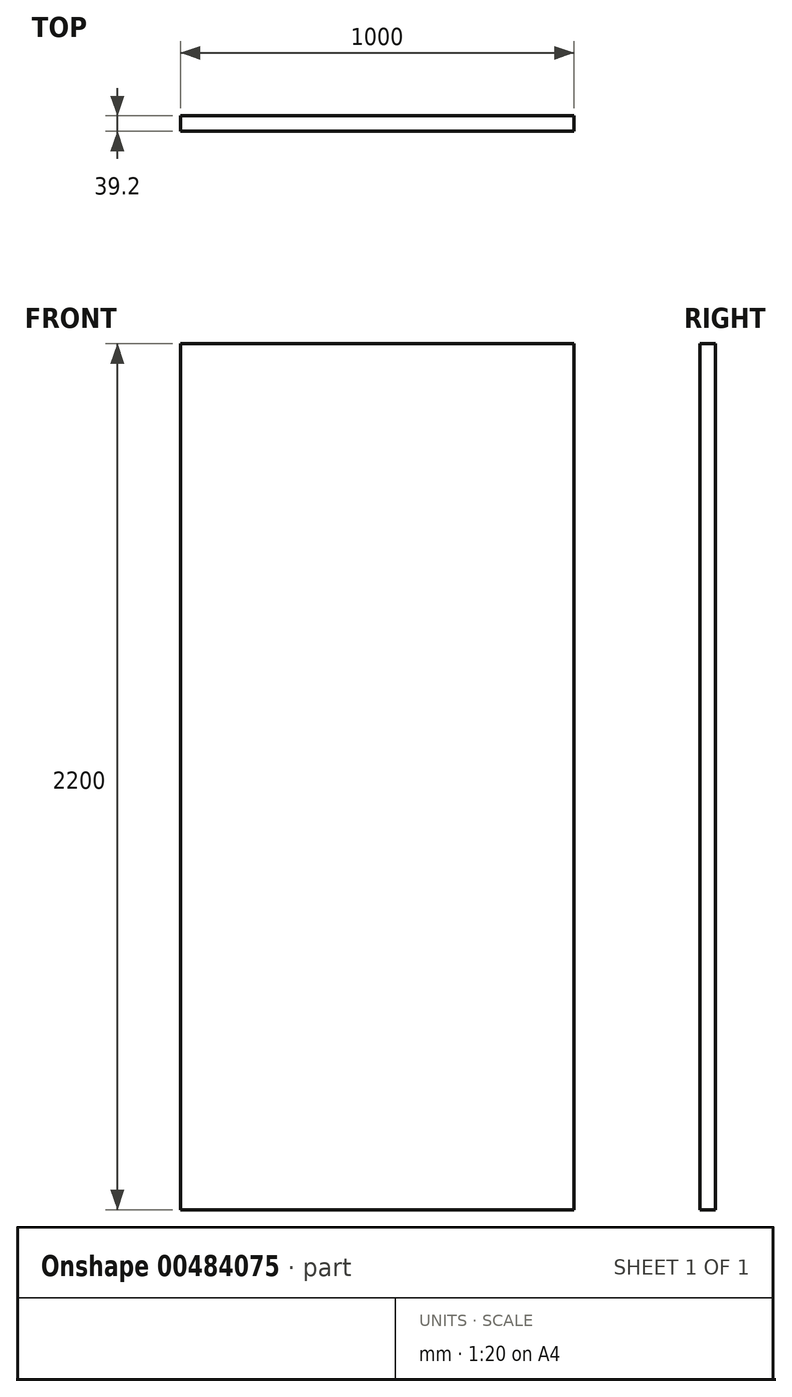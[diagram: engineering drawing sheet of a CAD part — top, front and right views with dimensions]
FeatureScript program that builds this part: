
annotation { "Feature Type Name" : "Feature", "Feature Type Description" : "" }
export const myFeature = defineFeature(function(context is Context, id is Id, definition is map)
    precondition{}
    {
        {
            var Q0;
            Q0=qCreatedBy(makeId("Top.planeOp"),FACE);
            var sketch = newSketch(context, id + "F0", { "sketchPlane" : qUnion([Q0])});
            skLineSegment(sketch, "E0.bottom", {"start": v(-87.13, -9.76) * mm, "end": v(912.87, -9.76) * mm});
            skLineSegment(sketch, "E0.top", {"start": v(-87.13, -48.96) * mm, "end": v(912.87, -48.96) * mm});
            skLineSegment(sketch, "E0.left", {"start": v(-87.13, -9.76) * mm, "end": v(-87.13, -48.96) * mm});
            skLineSegment(sketch, "E0.right", {"start": v(912.87, -9.76) * mm, "end": v(912.87, -48.96) * mm});
            skSolve(sketch);
        }
        {
            var Q0;
            Q0 = qSketchRegion(id + "F0", true);
            extrude(context, id + "F1", {"entities" : qUnion([Q0]), "depth" : 2200 * mm});
        }
    });
